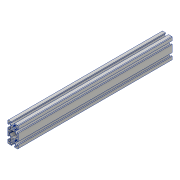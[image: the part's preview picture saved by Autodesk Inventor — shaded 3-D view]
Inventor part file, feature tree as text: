
AUTODESK INVENTOR PART (.ipt)
format: ipt  version: 2018 (Build 220112000, 112)  size: 243,712 bytes
history: native  units: mm
features: extrude x1, sketch x1
ambient origin geometry x8: Origin, YZ Plane, XZ Plane, XY Plane, X Axis, Y Axis, Z Axis, Center Point
bodies: Solid1 (feature_tree)
feature tree (2):
  extrude  "Extrusion1"  [1 undecoded]
  sketch  "Sketch1"  dims[d0=300.0mm d1=0.0mm]
note: 1 required parameter value undecoded (feature->parameter linkage not recoverable at this tier; creation-order binding heuristic only, values carry confidence <= 0.55)
